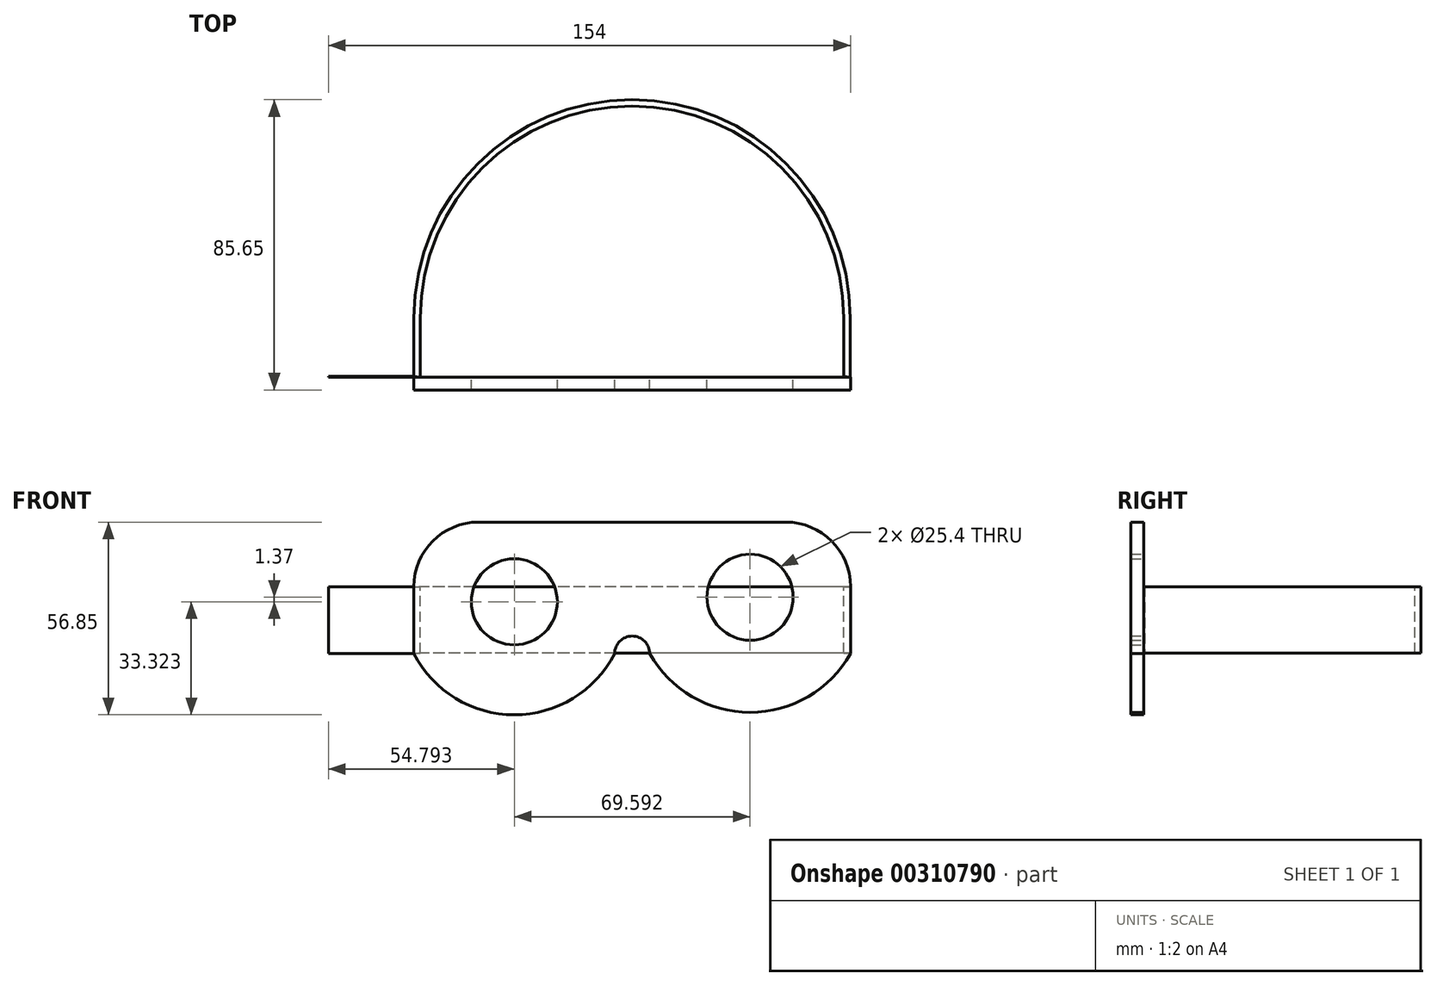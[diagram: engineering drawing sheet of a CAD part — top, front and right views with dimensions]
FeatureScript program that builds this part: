
annotation { "Feature Type Name" : "Feature", "Feature Type Description" : "" }
export const myFeature = defineFeature(function(context is Context, id is Id, definition is map)
    precondition{}
    {
        {
            var Q0;
            Q0=qCreatedBy(makeId("Front.planeOp"),FACE);
            var sketch = newSketch(context, id + "F0", { "sketchPlane" : qUnion([Q0])});
            skLineSegment(sketch, "E0", {"start": v(-67, 12.61) * mm, "end": v(61.8, 12.61) * mm});
            skLineSegment(sketch, "E1", {"start": v(-67, 12.61) * mm, "end": v(-67, -26.19) * mm});
            skPoint(sketch, "E2.startSnap0", {"position": v(-2.6, 12.61) * mm});
            skLineSegment(sketch, "E3", {"start": v(61.8, 12.61) * mm, "end": v(61.8, -26.19) * mm});
            skArc(sketch, "E4", {"start": v(2.58, -26.19) * mm, "mid": v(-2.6, -21) * mm, "end": v(-7.79, -26.19) * mm});
            skArc(sketch, "E5", {"start": v(-67, -26.19) * mm, "mid": v(-37.4, -44.24) * mm, "end": v(-7.79, -26.19) * mm});
            skArc(sketch, "E6", {"start": v(2.58, -26.19) * mm, "mid": v(32.2, -43.52) * mm, "end": v(61.8, -26.19) * mm});
            skCircle(sketch, "E7", {"center": v(-37.4, -10.92) * mm, "radius": 12.7 * mm});
            skCircle(sketch, "E8", {"center": v(32.2, -9.55) * mm, "radius": 12.7 * mm});
            skSolve(sketch);
        }
        {
            var Q0;
            Q0 = qSketchRegion(id + "F0", true);
            extrude(context, id + "F1", {"entities" : qUnion([Q0]), "depth" : 3.8 * mm});
        }
        {
            var Q0;
            Q0=makeQuery(id+"F1.opExtrude","SWEPT_EDGE",EDGE,{"disambiguationData":[OSD([sQuery(id+"F0.wireOp",EDGE,"E0"),sQuery(id+"F0.wireOp",EDGE,"E1")])]});
            var Q1;
            Q1=makeQuery(id+"F1.opExtrude","SWEPT_EDGE",EDGE,{"disambiguationData":[OSD([sQuery(id+"F0.wireOp",EDGE,"E0"),sQuery(id+"F0.wireOp",EDGE,"E3")])]});
            fillet(context, id + "F2", {"entities" : qUnion([Q0, Q1]), "radius" : 19.05 * mm, "tangentPropagation" : true, "allowEdgeOverflow" : false});
        }
        {
            var Q0;
            Q0=makeQuery(id+"F1.opExtrude","CAP_FACE",FACE,{"disambiguationData":[OSD([sQuery(id+"F0.wireOp",EDGE,"E0"),sQuery(id+"F0.wireOp",EDGE,"E1"),sQuery(id+"F0.wireOp",EDGE,"E3"),sQuery(id+"F0.wireOp",EDGE,"E4"),sQuery(id+"F0.wireOp",EDGE,"E5"),sQuery(id+"F0.wireOp",EDGE,"E6"),sQuery(id+"F0.wireOp",EDGE,"E7"),sQuery(id+"F0.wireOp",EDGE,"E8")])],"isStart":true});
            var sketch = newSketch(context, id + "F3", { "sketchPlane" : qUnion([Q0])});
            skLineSegment(sketch, "E9", {"start": v(67, -6.44) * mm, "end": v(92.2, -6.44) * mm});
            skLineSegment(sketch, "E10", {"start": v(92.2, -6.44) * mm, "end": v(92.2, -26.19) * mm});
            skLineSegment(sketch, "E11", {"start": v(92.2, -26.19) * mm, "end": v(67, -26.19) * mm});
            skSolve(sketch);
        }
        {
            var Q0;
            Q0=makeQuery(id+"F3.imprint","IMPRINT",FACE,{"disambiguationData":[TD([[makeQuery(id+"F3.imprint","IMPRINT",EDGE,{"derivedFrom":sQuery(id+"F3.wireOp",EDGE,"E9")}),-1.0]])]});
            extrude(context, id + "F4", {"entities" : qUnion([Q0]), "depth" : 0.25 * mm});
        }
        {
            var Q0;
            Q0=makeQuery(id+"F4.opExtrude","SWEPT_FACE",FACE,{"disambiguationData":[OSD([sQuery(id+"F3.wireOp",EDGE,"E9")])]});
            var sketch = newSketch(context, id + "F5", { "sketchPlane" : qUnion([Q0])});
            skLineSegment(sketch, "E12", {"start": v(-67, 0.25) * mm, "end": v(-67, 17.48) * mm});
            skLineSegment(sketch, "E13", {"start": v(61.7, 0) * mm, "end": v(61.7, 17.48) * mm});
            skArc(sketch, "E14", {"start": v(61.7, 17.48) * mm, "mid": v(-2.65, 81.84) * mm, "end": v(-67, 17.48) * mm});
            skLineSegment(sketch, "E15", {"start": v(-65.12, 0) * mm, "end": v(-65.12, 17.48) * mm});
            skLineSegment(sketch, "E16", {"start": v(59.82, 0.25) * mm, "end": v(59.82, 17.48) * mm});
            skArc(sketch, "E17", {"start": v(59.82, 17.48) * mm, "mid": v(-2.65, 79.95) * mm, "end": v(-65.12, 17.48) * mm});
            skLineSegment(sketch, "E18", {"start": v(-67, 0.25) * mm, "end": v(-65.12, 0) * mm});
            skLineSegment(sketch, "E19", {"start": v(59.82, 0.25) * mm, "end": v(61.7, 0) * mm});
            skSolve(sketch);
        }
        {
            var Q0;
            Q0 = qSketchRegion(id + "F5", true);
            extrude(context, id + "F6", {"entities" : qUnion([Q0]), "oppositeDirection" : true, "depth" : 19.56 * mm});
        }
    });
